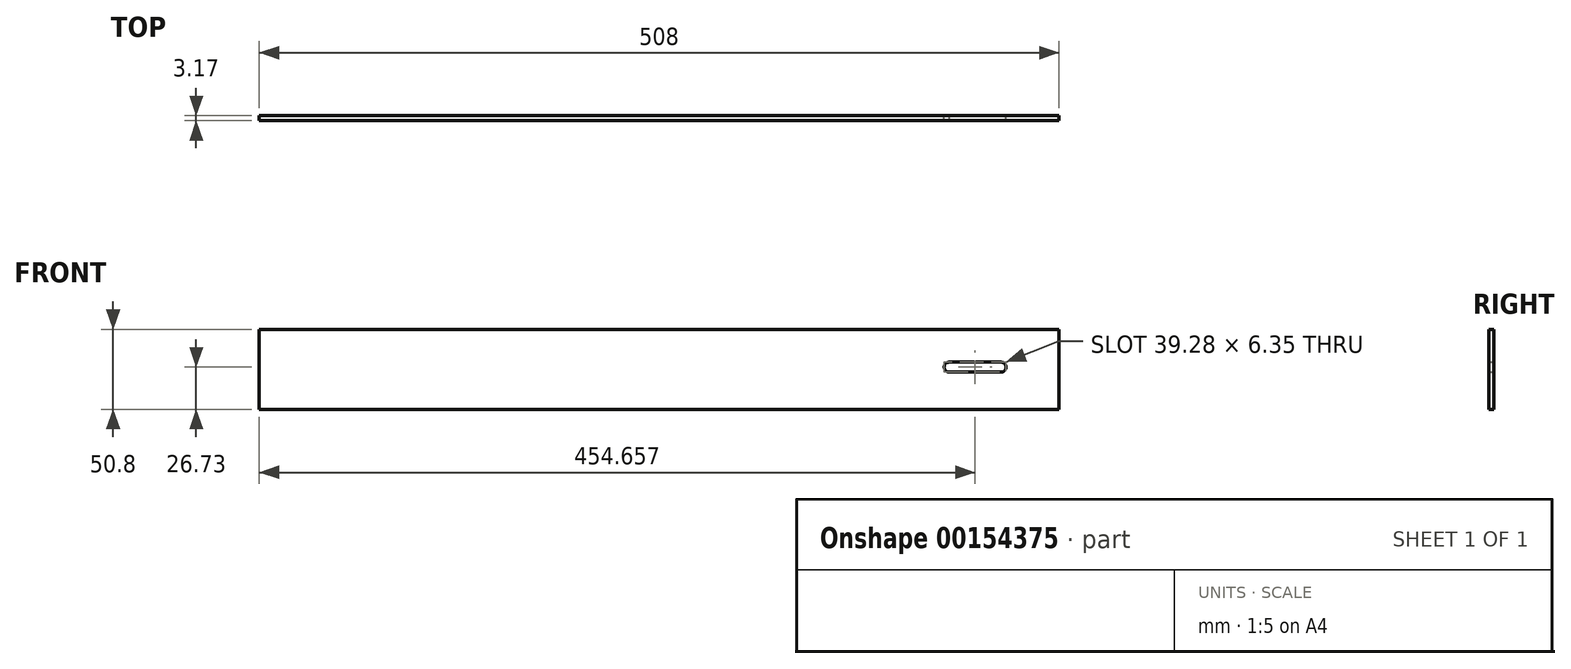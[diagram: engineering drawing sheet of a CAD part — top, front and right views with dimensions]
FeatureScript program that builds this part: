
annotation { "Feature Type Name" : "Feature", "Feature Type Description" : "" }
export const myFeature = defineFeature(function(context is Context, id is Id, definition is map)
    precondition{}
    {
        {
            var Q0;
            Q0=qCreatedBy(makeId("Front.planeOp"),FACE);
            var sketch = newSketch(context, id + "F0", { "sketchPlane" : qUnion([Q0])});
            skLineSegment(sketch, "E0.bottom", {"start": v(-451.68, 34.34) * mm, "end": v(56.32, 34.34) * mm});
            skLineSegment(sketch, "E0.top", {"start": v(-451.68, -16.46) * mm, "end": v(56.32, -16.46) * mm});
            skLineSegment(sketch, "E0.left", {"start": v(-451.68, 34.34) * mm, "end": v(-451.68, -16.46) * mm});
            skLineSegment(sketch, "E0.right", {"start": v(56.32, 34.34) * mm, "end": v(56.32, -16.46) * mm});
            skLineSegment(sketch, "E1", {"start": v(-451.68, 10.27) * mm, "end": v(-16.67, 10.27) * mm});
            skArc(sketch, "E2", {"start": v(19.44, 7.1) * mm, "mid": v(22.62, 10.27) * mm, "end": v(19.44, 13.44) * mm});
            skArc(sketch, "E3", {"start": v(-13.24, 13.43) * mm, "mid": v(-16.67, 10.4) * mm, "end": v(-13.5, 7.1) * mm});
            skLineSegment(sketch, "E4", {"start": v(-13.75, 13.43) * mm, "end": v(19.44, 13.44) * mm});
            skLineSegment(sketch, "E5", {"start": v(19.44, 7.1) * mm, "end": v(-13.5, 7.1) * mm});
            skSolve(sketch);
        }
        {
            var Q0;
            Q0 = qSketchRegion(id + "F0", true);
            extrude(context, id + "F1", {"entities" : qUnion([Q0]), "depth" : 3.17 * mm});
        }
    });
